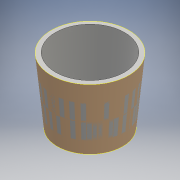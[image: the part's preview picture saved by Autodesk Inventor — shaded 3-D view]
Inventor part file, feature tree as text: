
AUTODESK INVENTOR PART (.ipt)
format: ipt  version: 2016 (Build 200138000, 138)  size: 120,832 bytes
history: native  units: mm
features: sketch x2, plane x1, thicken_offset x1, other x1, loft x1
ambient origin geometry x8: Origin, YZ Plane, XZ Plane, XY Plane, X Axis, Y Axis, Z Axis, Center Point
bodies: Body1 (feature_tree), Body2 (feature_tree)
feature tree (6):
  sketch  "Sketch1"  dims[d0=168.0mm d1=9.52mm]
  plane  "Work Plane1"
  thicken_offset  "Thicken1"
  sketch  "Sketch2"  dims[d2=-140.0mm d3=141.0mm d4=9.52mm d15=0.0mm d16=90.0deg d17=0.0mm d18=90.0deg d19=9.52mm d20=9.52mm]
  other  "Srf1"
  loft  "LoftSrf1"
